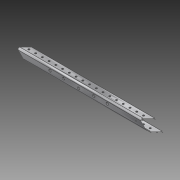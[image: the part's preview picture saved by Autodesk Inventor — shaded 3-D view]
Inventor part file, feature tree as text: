
AUTODESK INVENTOR PART (.ipt)
format: ipt  version: 2014 SP1 (Build 180222100, 222)  size: 214,528 bytes
history: native  units: in
note: dims shown in document units (in); Inventor stores cm internally (conversion verified against a paired STEP export)
features: sketch x6, extrude x4, hole x3, pattern_linear x1, reference x1
ambient origin geometry x8: Origin, YZ Plane, XZ Plane, XY Plane, X Axis, Y Axis, Z Axis, Center Point
bodies: Solid1 (feature_tree)
feature tree (15):
  extrude  "Extrusion1"  Depth=0.125in
  sketch  "Sketch2"  dims[d2=1.0in d3=1.0in]
  hole  "Hole1"  [1 undecoded]
  hole  "Hole2"  [1 undecoded]
  hole  "Hole3"  [1 undecoded]
  pattern_linear  "Rectangular Pattern1"  Count1=2 Spacing1=10.0in
  extrude  "Extrusion2"  Depth=1.0in
  extrude  "Extrusion3"  Depth=1.0in
  extrude  "Extrusion4"  Depth=1.0in
  sketch  "Sketch1"  dims[d0=1.125in d1=0.125in]
  sketch  "Sketch3"  dims[d4=0.125in d5=0.125in]
  sketch  "Sketch4"  dims[d6=0.25in d7=35.0in d8=0.0in]
  sketch  "Sketch5"  dims[d10=0.3in]
  sketch  "Sketch6"  dims[d11=0.15in d12=0.7874in d14=10.0in d15=0.3937in d17=1.0in d20=0.38in d21=0.75in d22=0.375in d23=0.25in d24=0.5635in d25=1.0in d26=0.8108in d27=0.125in d28=0.75in d29=0.375in d30=0.25in d31=0.5635in d32=1.0in d33=0.8108in d34=0.5in d35=0.5in d36=0.257in d37=0.75in d38=0.375in d39=0.25in d40=0.5635in d41=1.0in d42=0.8108in d43=13.7795in d45=1.0in d46=4.75in d47=0.0in d48=7.0in d49=0.0in d50=1.0in d51=0.0in]
  reference  "Reference1"
note: 3 required parameter values undecoded (feature->parameter linkage not recoverable at this tier; creation-order binding heuristic only, values carry confidence <= 0.55)
